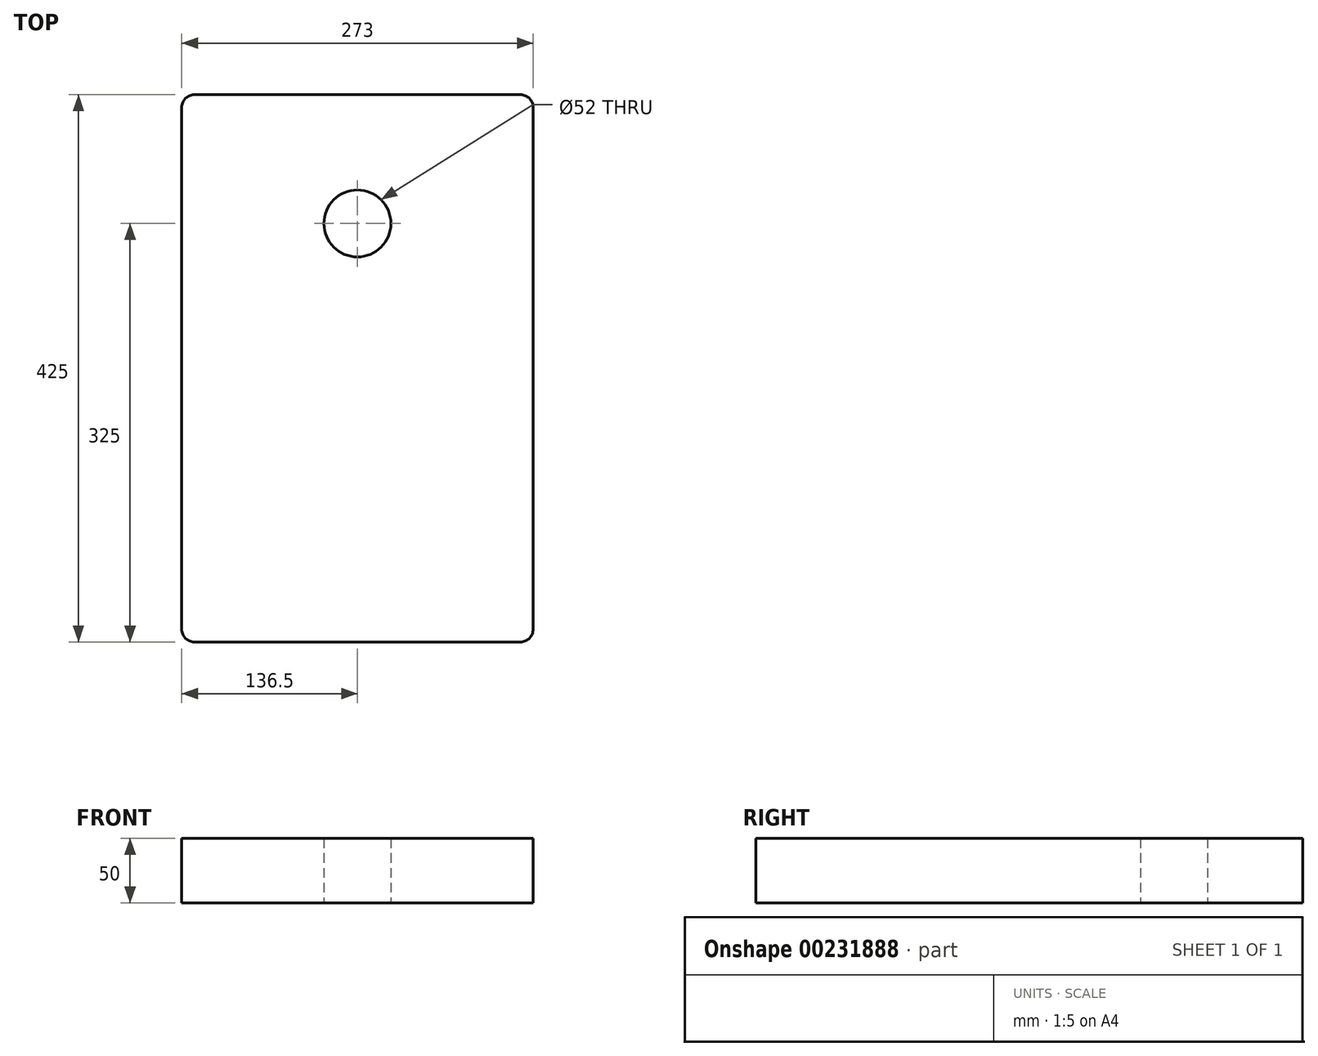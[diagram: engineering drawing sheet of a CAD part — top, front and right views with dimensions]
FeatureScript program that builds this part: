
annotation { "Feature Type Name" : "Feature", "Feature Type Description" : "" }
export const myFeature = defineFeature(function(context is Context, id is Id, definition is map)
    precondition{}
    {
        {
            var Q0;
            Q0=qCreatedBy(makeId("Top.planeOp"),FACE);
            var sketch = newSketch(context, id + "F0", { "sketchPlane" : qUnion([Q0])});
            skLineSegment(sketch, "E0.bottom", {"start": v(10, 0) * mm, "end": v(263, 0) * mm});
            skLineSegment(sketch, "E0.top", {"start": v(10, 425) * mm, "end": v(263, 425) * mm});
            skLineSegment(sketch, "E0.left", {"start": v(0, 10) * mm, "end": v(0, 415) * mm});
            skLineSegment(sketch, "E0.right", {"start": v(273, 10) * mm, "end": v(273, 415) * mm});
            skCircle(sketch, "E1", {"center": v(136.5, 325) * mm, "radius": 26 * mm});
            skPoint(sketch, "E2.visualSharp", {"position": v(0, 0) * mm});
            skArc(sketch, "E2.filletArc", {"start": v(0, 10) * mm, "mid": v(2.93, 2.93) * mm, "end": v(10, 0) * mm});
            skPoint(sketch, "E3.visualSharp", {"position": v(273, 0) * mm});
            skArc(sketch, "E3.filletArc", {"start": v(263, 0) * mm, "mid": v(270.07, 2.93) * mm, "end": v(273, 10) * mm});
            skPoint(sketch, "E4.visualSharp", {"position": v(273, 425) * mm});
            skArc(sketch, "E4.filletArc", {"start": v(273, 415) * mm, "mid": v(270.07, 422.07) * mm, "end": v(263, 425) * mm});
            skPoint(sketch, "E5.visualSharp", {"position": v(0, 425) * mm});
            skArc(sketch, "E5.filletArc", {"start": v(10, 425) * mm, "mid": v(2.93, 422.07) * mm, "end": v(0, 415) * mm});
            skSolve(sketch);
        }
        {
            var Q0;
            Q0 = qSketchRegion(id + "F0", true);
            extrude(context, id + "F1", {"entities" : qUnion([Q0]), "depth" : 50 * mm});
        }
    });
